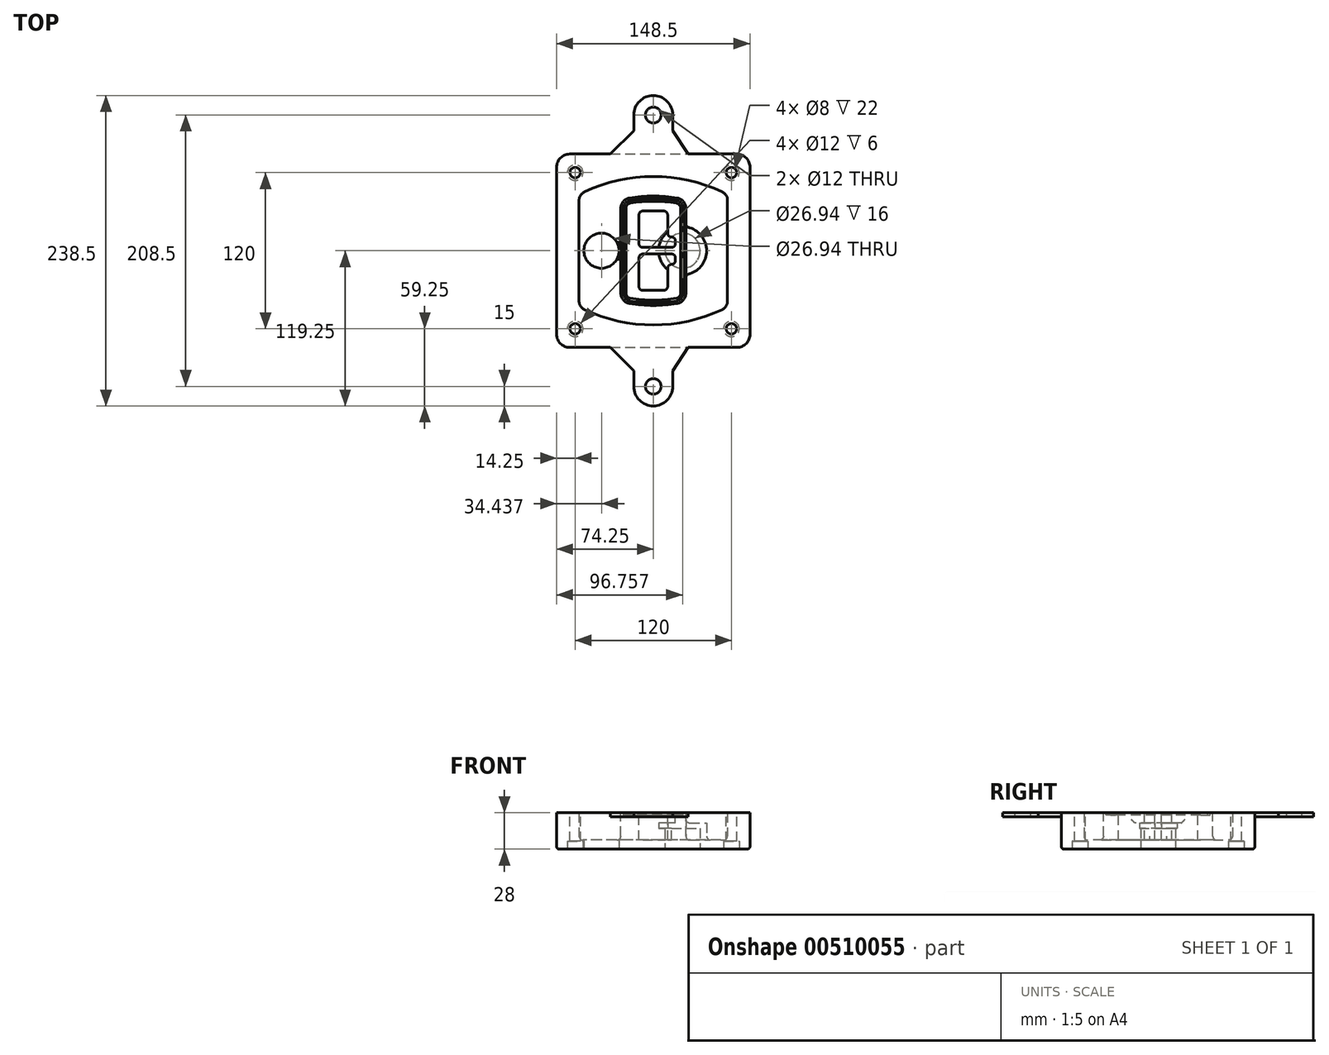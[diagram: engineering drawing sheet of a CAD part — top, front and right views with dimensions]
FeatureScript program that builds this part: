
annotation { "Feature Type Name" : "Feature", "Feature Type Description" : "" }
export const myFeature = defineFeature(function(context is Context, id is Id, definition is map)
    precondition{}
    {
        {
            var Q0;
            Q0=qCreatedBy(makeId("Top.planeOp"),FACE);
            var sketch = newSketch(context, id + "F0", { "sketchPlane" : qUnion([Q0])});
            skPoint(sketch, "E0.rect.middle", {"position": v(0, 0) * mm});
            skLineSegment(sketch, "E1.bottom", {"start": v(-64.25, -74.25) * mm, "end": v(64.25, -74.25) * mm});
            skLineSegment(sketch, "E1.top", {"start": v(-64.25, 74.25) * mm, "end": v(64.25, 74.25) * mm});
            skLineSegment(sketch, "E1.left", {"start": v(-74.25, -64.25) * mm, "end": v(-74.25, 64.25) * mm});
            skLineSegment(sketch, "E1.right", {"start": v(74.25, -64.25) * mm, "end": v(74.25, 64.25) * mm});
            skLineSegment(sketch, "E2", {"start": v(-74.25, 74.25) * mm, "end": v(74.25, -74.25) * mm, "construction": true});
            skLineSegment(sketch, "E3", {"start": v(74.25, 74.25) * mm, "end": v(-74.25, -74.25) * mm, "construction": true});
            skCircle(sketch, "E4", {"center": v(-60, 60) * mm, "radius": 4 * mm});
            skCircle(sketch, "E5", {"center": v(60, 60) * mm, "radius": 4 * mm});
            skCircle(sketch, "E6", {"center": v(60, -60) * mm, "radius": 4 * mm});
            skCircle(sketch, "E7", {"center": v(-60, -60) * mm, "radius": 4 * mm});
            skLineSegment(sketch, "E8", {"start": v(-60, 60) * mm, "end": v(60, 60) * mm, "construction": true});
            skLineSegment(sketch, "E9", {"start": v(60, 60) * mm, "end": v(60, -60) * mm, "construction": true});
            skLineSegment(sketch, "E10", {"start": v(60, -60) * mm, "end": v(-60, -60) * mm, "construction": true});
            skLineSegment(sketch, "E11", {"start": v(-60, -60) * mm, "end": v(-60, 60) * mm, "construction": true});
            skLineSegment(sketch, "E12", {"start": v(-60, 38.83) * mm, "end": v(-60, -38.83) * mm});
            skLineSegment(sketch, "E13", {"start": v(60, 38.83) * mm, "end": v(60, -38.83) * mm});
            skArc(sketch, "E14", {"start": v(54.26, 47.88) * mm, "mid": v(0, 60) * mm, "end": v(-54.26, 47.88) * mm});
            skArc(sketch, "E15", {"start": v(-54.26, -47.88) * mm, "mid": v(0, -60) * mm, "end": v(54.26, -47.88) * mm});
            skLineSegment(sketch, "E16", {"start": v(-60, 0) * mm, "end": v(60, 0) * mm, "construction": true});
            skPoint(sketch, "E17.visualSharp", {"position": v(-60, -45) * mm});
            skArc(sketch, "E17.filletArc", {"start": v(-60, -38.83) * mm, "mid": v(-58.44, -44.2) * mm, "end": v(-54.26, -47.88) * mm});
            skPoint(sketch, "E18.visualSharp", {"position": v(-60, 45) * mm});
            skArc(sketch, "E18.filletArc", {"start": v(-54.26, 47.88) * mm, "mid": v(-58.44, 44.2) * mm, "end": v(-60, 38.83) * mm});
            skPoint(sketch, "E19.visualSharp", {"position": v(60, 45) * mm});
            skArc(sketch, "E19.filletArc", {"start": v(60, 38.83) * mm, "mid": v(58.44, 44.2) * mm, "end": v(54.26, 47.88) * mm});
            skPoint(sketch, "E20.visualSharp", {"position": v(60, -45) * mm});
            skArc(sketch, "E20.filletArc", {"start": v(54.26, -47.88) * mm, "mid": v(58.44, -44.2) * mm, "end": v(60, -38.83) * mm});
            skPoint(sketch, "E21.visualSharp", {"position": v(-74.25, 74.25) * mm});
            skArc(sketch, "E21.filletArc", {"start": v(-64.25, 74.25) * mm, "mid": v(-71.32, 71.32) * mm, "end": v(-74.25, 64.25) * mm});
            skPoint(sketch, "E22.visualSharp", {"position": v(74.25, 74.25) * mm});
            skArc(sketch, "E22.filletArc", {"start": v(74.25, 64.25) * mm, "mid": v(71.32, 71.32) * mm, "end": v(64.25, 74.25) * mm});
            skPoint(sketch, "E23.visualSharp", {"position": v(74.25, -74.25) * mm});
            skArc(sketch, "E23.filletArc", {"start": v(64.25, -74.25) * mm, "mid": v(71.32, -71.32) * mm, "end": v(74.25, -64.25) * mm});
            skPoint(sketch, "E24.visualSharp", {"position": v(-74.25, -74.25) * mm});
            skArc(sketch, "E24.filletArc", {"start": v(-74.25, -64.25) * mm, "mid": v(-71.32, -71.32) * mm, "end": v(-64.25, -74.25) * mm});
            skArc(sketch, "E25.0", {"start": v(57, 38.83) * mm, "mid": v(55.9, 42.58) * mm, "end": v(52.98, 45.17) * mm});
            skLineSegment(sketch, "E25.1", {"start": v(57, 38.83) * mm, "end": v(57, -38.83) * mm});
            skArc(sketch, "E25.2", {"start": v(52.98, -45.17) * mm, "mid": v(55.9, -42.58) * mm, "end": v(57, -38.83) * mm});
            skArc(sketch, "E25.3", {"start": v(-52.98, -45.17) * mm, "mid": v(0, -57) * mm, "end": v(52.98, -45.17) * mm});
            skArc(sketch, "E25.4", {"start": v(-57, -38.83) * mm, "mid": v(-55.9, -42.58) * mm, "end": v(-52.98, -45.17) * mm});
            skArc(sketch, "E25.5", {"start": v(52.98, 45.17) * mm, "mid": v(0, 57) * mm, "end": v(-52.98, 45.17) * mm});
            skLineSegment(sketch, "E25.6", {"start": v(-57, 38.83) * mm, "end": v(-57, -38.83) * mm});
            skArc(sketch, "E25.7", {"start": v(-52.98, 45.17) * mm, "mid": v(-55.9, 42.58) * mm, "end": v(-57, 38.83) * mm});
            skArc(sketch, "E26.0", {"start": v(-55.96, 51.5) * mm, "mid": v(-61.82, 46.33) * mm, "end": v(-64, 38.83) * mm});
            skArc(sketch, "E26.1", {"start": v(55.96, 51.5) * mm, "mid": v(0, 64) * mm, "end": v(-55.96, 51.5) * mm});
            skArc(sketch, "E26.2", {"start": v(64, 38.83) * mm, "mid": v(61.82, 46.33) * mm, "end": v(55.96, 51.5) * mm});
            skLineSegment(sketch, "E26.3", {"start": v(64, 38.83) * mm, "end": v(64, -38.83) * mm});
            skArc(sketch, "E26.4", {"start": v(55.96, -51.5) * mm, "mid": v(61.82, -46.33) * mm, "end": v(64, -38.83) * mm});
            skLineSegment(sketch, "E26.5", {"start": v(-64, 38.83) * mm, "end": v(-64, -38.83) * mm});
            skArc(sketch, "E26.6", {"start": v(-55.96, -51.5) * mm, "mid": v(0, -64) * mm, "end": v(55.96, -51.5) * mm});
            skArc(sketch, "E26.7", {"start": v(-64, -38.83) * mm, "mid": v(-61.82, -46.33) * mm, "end": v(-55.96, -51.5) * mm});
            skSolve(sketch);
        }
        {
            var Q0;
            Q0=makeQuery(id+"F0.imprint","IMPRINT",FACE,{"disambiguationData":[TD([[makeQuery(id+"F0.imprint","IMPRINT",EDGE,{"derivedFrom":sQuery(id+"F0.wireOp",EDGE,"E1.bottom")}),1.0]])]});
            var Q1;
            Q1=makeQuery(id+"F0.imprint","IMPRINT",FACE,{"disambiguationData":[TD([[makeQuery(id+"F0.imprint","IMPRINT",EDGE,{"derivedFrom":sQuery(id+"F0.wireOp",EDGE,"E12")}),1.0]])]});
            var Q2;
            Q2=makeQuery(id+"F0.imprint","IMPRINT",FACE,{"disambiguationData":[TD([[makeQuery(id+"F0.imprint","IMPRINT",EDGE,{"derivedFrom":sQuery(id+"F0.wireOp",EDGE,"E25.0")}),1.0]])]});
            var Q3;
            Q3=makeQuery(id+"F0.imprint","IMPRINT",FACE,{"disambiguationData":[TD([[makeQuery(id+"F0.imprint","IMPRINT",EDGE,{"derivedFrom":sQuery(id+"F0.wireOp",EDGE,"E12")}),-1.0]])]});
            extrude(context, id + "F1", {"entities" : qUnion([Q0, Q1, Q2, Q3]), "oppositeDirection" : true, "depth" : 25 * mm});
        }
        {
            var Q0;
            Q0=makeQuery(id+"F0.imprint","IMPRINT",FACE,{"disambiguationData":[TD([[makeQuery(id+"F0.imprint","IMPRINT",EDGE,{"derivedFrom":sQuery(id+"F0.wireOp",EDGE,"E12")}),1.0]])]});
            extrude(context, id + "F2", {"entities" : qUnion([Q0]), "operationType" : NewBodyOperationType.ADD, "depth" : 3 * mm});
        }
        {
            var Q0;
            Q0=makeQuery(id+"F0.imprint","IMPRINT",FACE,{"disambiguationData":[TD([[makeQuery(id+"F0.imprint","IMPRINT",EDGE,{"derivedFrom":sQuery(id+"F0.wireOp",EDGE,"E25.0")}),1.0]])]});
            extrude(context, id + "F3", {"entities" : qUnion([Q0]), "operationType" : NewBodyOperationType.REMOVE, "oppositeDirection" : true, "depth" : 18 * mm});
        }
        {
            var Q0;
            Q0=makeQuery(id+"F2.opExtrude","CAP_FACE",FACE,{"disambiguationData":[OSD([sQuery(id+"F0.wireOp",EDGE,"E12"),sQuery(id+"F0.wireOp",EDGE,"E13"),sQuery(id+"F0.wireOp",EDGE,"E14"),sQuery(id+"F0.wireOp",EDGE,"E15"),sQuery(id+"F0.wireOp",EDGE,"E17.filletArc"),sQuery(id+"F0.wireOp",EDGE,"E18.filletArc"),sQuery(id+"F0.wireOp",EDGE,"E19.filletArc"),sQuery(id+"F0.wireOp",EDGE,"E20.filletArc"),sQuery(id+"F0.wireOp",EDGE,"E25.0"),sQuery(id+"F0.wireOp",EDGE,"E25.1"),sQuery(id+"F0.wireOp",EDGE,"E25.2"),sQuery(id+"F0.wireOp",EDGE,"E25.3"),sQuery(id+"F0.wireOp",EDGE,"E25.4"),sQuery(id+"F0.wireOp",EDGE,"E25.5"),sQuery(id+"F0.wireOp",EDGE,"E25.6"),sQuery(id+"F0.wireOp",EDGE,"E25.7")])],"isStart":false});
            var sketch = newSketch(context, id + "F4", { "sketchPlane" : qUnion([Q0])});
            skArc(sketch, "E27.0", {"start": v(-18.34, -40.45) * mm, "mid": v(0, -42) * mm, "end": v(18.34, -40.45) * mm});
            skArc(sketch, "E28.0", {"start": v(18.34, 40.45) * mm, "mid": v(0, 42) * mm, "end": v(-18.34, 40.45) * mm});
            skLineSegment(sketch, "E29", {"start": v(-25, 32.57) * mm, "end": v(-25, -32.57) * mm});
            skLineSegment(sketch, "E30", {"start": v(25, 32.57) * mm, "end": v(25, -32.57) * mm});
            skLineSegment(sketch, "E31", {"start": v(-25, 39.1) * mm, "end": v(25, 39.1) * mm, "construction": true});
            skLineSegment(sketch, "E32", {"start": v(-25, -39.1) * mm, "end": v(25, -39.1) * mm, "construction": true});
            skPoint(sketch, "E33.visualSharp", {"position": v(-25, 39.1) * mm});
            skArc(sketch, "E33.filletArc", {"start": v(-18.34, 40.45) * mm, "mid": v(-23.11, 37.73) * mm, "end": v(-25, 32.57) * mm});
            skPoint(sketch, "E34.visualSharp", {"position": v(25, 39.1) * mm});
            skArc(sketch, "E34.filletArc", {"start": v(25, 32.57) * mm, "mid": v(23.11, 37.73) * mm, "end": v(18.34, 40.45) * mm});
            skPoint(sketch, "E35.visualSharp", {"position": v(25, -39.1) * mm});
            skArc(sketch, "E35.filletArc", {"start": v(18.34, -40.45) * mm, "mid": v(23.11, -37.73) * mm, "end": v(25, -32.57) * mm});
            skPoint(sketch, "E36.visualSharp", {"position": v(-25, -39.1) * mm});
            skArc(sketch, "E36.filletArc", {"start": v(-25, -32.57) * mm, "mid": v(-23.11, -37.73) * mm, "end": v(-18.34, -40.45) * mm});
            skArc(sketch, "E37.0", {"start": v(52.98, 45.17) * mm, "mid": v(0, 57) * mm, "end": v(-52.98, 45.17) * mm});
            skArc(sketch, "E37.1", {"start": v(-52.98, 45.17) * mm, "mid": v(-55.9, 42.58) * mm, "end": v(-57, 38.83) * mm});
            skLineSegment(sketch, "E37.2", {"start": v(-57, 38.83) * mm, "end": v(-57, -38.83) * mm});
            skArc(sketch, "E37.3", {"start": v(-57, -38.83) * mm, "mid": v(-55.9, -42.58) * mm, "end": v(-52.98, -45.17) * mm});
            skArc(sketch, "E37.4", {"start": v(-52.98, -45.17) * mm, "mid": v(0, -57) * mm, "end": v(52.98, -45.17) * mm});
            skArc(sketch, "E37.5", {"start": v(52.98, -45.17) * mm, "mid": v(55.9, -42.58) * mm, "end": v(57, -38.83) * mm});
            skLineSegment(sketch, "E37.6", {"start": v(57, 38.83) * mm, "end": v(57, -38.83) * mm});
            skArc(sketch, "E37.7", {"start": v(57, 38.83) * mm, "mid": v(55.9, 42.58) * mm, "end": v(52.98, 45.17) * mm});
            skLineSegment(sketch, "E38.0", {"start": v(23, 32.57) * mm, "end": v(23, -32.57) * mm});
            skArc(sketch, "E38.1", {"start": v(18, -38.48) * mm, "mid": v(21.58, -36.44) * mm, "end": v(23, -32.57) * mm});
            skArc(sketch, "E38.2", {"start": v(-18, -38.48) * mm, "mid": v(0, -40) * mm, "end": v(18, -38.48) * mm});
            skArc(sketch, "E38.3", {"start": v(-23, -32.57) * mm, "mid": v(-21.58, -36.44) * mm, "end": v(-18, -38.48) * mm});
            skLineSegment(sketch, "E38.4", {"start": v(-23, 32.57) * mm, "end": v(-23, -32.57) * mm});
            skArc(sketch, "E38.5", {"start": v(23, 32.57) * mm, "mid": v(21.58, 36.44) * mm, "end": v(18, 38.48) * mm});
            skArc(sketch, "E38.6", {"start": v(-18, 38.48) * mm, "mid": v(-21.58, 36.44) * mm, "end": v(-23, 32.57) * mm});
            skArc(sketch, "E38.7", {"start": v(18, 38.48) * mm, "mid": v(0, 40) * mm, "end": v(-18, 38.48) * mm});
            skArc(sketch, "E39.0", {"start": v(21, 32.57) * mm, "mid": v(20.06, 35.15) * mm, "end": v(17.67, 36.5) * mm});
            skLineSegment(sketch, "E39.1", {"start": v(21, 32.57) * mm, "end": v(21, -32.57) * mm});
            skArc(sketch, "E39.2", {"start": v(17.67, -36.5) * mm, "mid": v(20.06, -35.15) * mm, "end": v(21, -32.57) * mm});
            skArc(sketch, "E39.3", {"start": v(-17.67, -36.5) * mm, "mid": v(0, -38) * mm, "end": v(17.67, -36.5) * mm});
            skArc(sketch, "E39.4", {"start": v(-21, -32.57) * mm, "mid": v(-20.06, -35.15) * mm, "end": v(-17.67, -36.5) * mm});
            skArc(sketch, "E39.5", {"start": v(17.67, 36.5) * mm, "mid": v(0, 38) * mm, "end": v(-17.67, 36.5) * mm});
            skLineSegment(sketch, "E39.6", {"start": v(-21, 32.57) * mm, "end": v(-21, -32.57) * mm});
            skArc(sketch, "E39.7", {"start": v(-17.67, 36.5) * mm, "mid": v(-20.06, 35.15) * mm, "end": v(-21, 32.57) * mm});
            skLineSegment(sketch, "E40", {"start": v(-25, 0) * mm, "end": v(25, 0) * mm, "construction": true});
            skLineSegment(sketch, "E41", {"start": v(-11, 5.5) * mm, "end": v(-11, 27.5) * mm});
            skLineSegment(sketch, "E42", {"start": v(-8, 30.5) * mm, "end": v(8, 30.5) * mm});
            skLineSegment(sketch, "E43", {"start": v(11, 27.5) * mm, "end": v(11, 13.5) * mm});
            skLineSegment(sketch, "E44", {"start": v(14, 10.5) * mm, "end": v(14, 10.5) * mm});
            skLineSegment(sketch, "E45", {"start": v(17, 7.5) * mm, "end": v(17, 5.5) * mm});
            skLineSegment(sketch, "E46", {"start": v(14, 2.5) * mm, "end": v(-8, 2.5) * mm});
            skPoint(sketch, "E47.visualSharp", {"position": v(-11, 30.5) * mm});
            skArc(sketch, "E47.filletArc", {"start": v(-8, 30.5) * mm, "mid": v(-10.12, 29.62) * mm, "end": v(-11, 27.5) * mm});
            skPoint(sketch, "E48.visualSharp", {"position": v(11, 30.5) * mm});
            skArc(sketch, "E48.filletArc", {"start": v(11, 27.5) * mm, "mid": v(10.12, 29.62) * mm, "end": v(8, 30.5) * mm});
            skPoint(sketch, "E49.visualSharp", {"position": v(11, 10.5) * mm});
            skArc(sketch, "E49.filletArc", {"start": v(11, 13.5) * mm, "mid": v(11.88, 11.38) * mm, "end": v(14, 10.5) * mm});
            skPoint(sketch, "E50.visualSharp", {"position": v(17, 10.5) * mm});
            skArc(sketch, "E50.filletArc", {"start": v(17, 7.5) * mm, "mid": v(16.12, 9.62) * mm, "end": v(14, 10.5) * mm});
            skPoint(sketch, "E51.visualSharp", {"position": v(17, 2.5) * mm});
            skArc(sketch, "E51.filletArc", {"start": v(14, 2.5) * mm, "mid": v(16.12, 3.38) * mm, "end": v(17, 5.5) * mm});
            skPoint(sketch, "E52.visualSharp", {"position": v(-11, 2.5) * mm});
            skArc(sketch, "E52.filletArc", {"start": v(-11, 5.5) * mm, "mid": v(-10.12, 3.38) * mm, "end": v(-8, 2.5) * mm});
            skLineSegment(sketch, "E53.0.MirrorCS", {"start": v(14, -2.5) * mm, "end": v(-8, -2.5) * mm});
            skArc(sketch, "E54.0.MirrorCS", {"start": v(-11, -5.5) * mm, "mid": v(-10.12, -3.38) * mm, "end": v(-8, -2.5) * mm});
            skLineSegment(sketch, "E55.0.MirrorCS", {"start": v(-11, -5.5) * mm, "end": v(-11, -27.5) * mm});
            skArc(sketch, "E56.0.MirrorCS", {"start": v(-8, -30.5) * mm, "mid": v(-10.12, -29.62) * mm, "end": v(-11, -27.5) * mm});
            skLineSegment(sketch, "E57.0.MirrorCS", {"start": v(-8, -30.5) * mm, "end": v(8, -30.5) * mm});
            skArc(sketch, "E58.0.MirrorCS", {"start": v(11, -27.5) * mm, "mid": v(10.12, -29.62) * mm, "end": v(8, -30.5) * mm});
            skLineSegment(sketch, "E59.0.MirrorCS", {"start": v(11, -27.5) * mm, "end": v(11, -13.5) * mm});
            skArc(sketch, "E60.0.MirrorCS", {"start": v(11, -13.5) * mm, "mid": v(11.88, -11.38) * mm, "end": v(14, -10.5) * mm});
            skArc(sketch, "E61.0.MirrorCS", {"start": v(17, -7.5) * mm, "mid": v(16.12, -9.62) * mm, "end": v(14, -10.5) * mm});
            skLineSegment(sketch, "E62.0.MirrorCS", {"start": v(17, -7.5) * mm, "end": v(17, -5.5) * mm});
            skArc(sketch, "E63.0.MirrorCS", {"start": v(14, -2.5) * mm, "mid": v(16.12, -3.38) * mm, "end": v(17, -5.5) * mm});
            skSolve(sketch);
        }
        {
            var Q0;
            Q0=makeQuery(id+"F4.imprint","IMPRINT",FACE,{"disambiguationData":[TD([[makeQuery(id+"F4.imprint","IMPRINT",EDGE,{"derivedFrom":sQuery(id+"F4.wireOp",EDGE,"E27.0")}),1.0]])]});
            var Q1;
            Q1=makeQuery(id+"F4.imprint","IMPRINT",FACE,{"disambiguationData":[TD([[makeQuery(id+"F4.imprint","IMPRINT",EDGE,{"derivedFrom":sQuery(id+"F4.wireOp",EDGE,"E38.0")}),-1.0]])]});
            var Q2;
            Q2=makeQuery(id+"F4.imprint","IMPRINT",FACE,{"disambiguationData":[TD([[makeQuery(id+"F4.imprint","IMPRINT",EDGE,{"derivedFrom":sQuery(id+"F4.wireOp",EDGE,"E39.0")}),1.0]])]});
            extrude(context, id + "F5", {"entities" : qUnion([Q0, Q1, Q2]), "operationType" : NewBodyOperationType.ADD, "endBound" : BoundingType.UP_TO_NEXT, "oppositeDirection" : true, "depth" : 25 * mm});
        }
        {
            var Q0;
            Q0=makeQuery(id+"F4.imprint","IMPRINT",FACE,{"disambiguationData":[TD([[makeQuery(id+"F4.imprint","IMPRINT",EDGE,{"derivedFrom":sQuery(id+"F4.wireOp",EDGE,"E38.0")}),-1.0]])]});
            extrude(context, id + "F6", {"entities" : qUnion([Q0]), "operationType" : NewBodyOperationType.REMOVE, "oppositeDirection" : true, "depth" : 2 * mm});
        }
        {
            var Q0;
            Q0=makeQuery(id+"F1.opExtrude","CAP_FACE",FACE,{"disambiguationData":[OSD([sQuery(id+"F0.wireOp",EDGE,"E1.bottom"),sQuery(id+"F0.wireOp",EDGE,"E1.top"),sQuery(id+"F0.wireOp",EDGE,"E1.left"),sQuery(id+"F0.wireOp",EDGE,"E1.right"),sQuery(id+"F0.wireOp",EDGE,"E4"),sQuery(id+"F0.wireOp",EDGE,"E5"),sQuery(id+"F0.wireOp",EDGE,"E6"),sQuery(id+"F0.wireOp",EDGE,"E7"),sQuery(id+"F0.wireOp",EDGE,"E21.filletArc"),sQuery(id+"F0.wireOp",EDGE,"E22.filletArc"),sQuery(id+"F0.wireOp",EDGE,"E23.filletArc"),sQuery(id+"F0.wireOp",EDGE,"E24.filletArc")])],"isStart":false});
            var sketch = newSketch(context, id + "F7", { "sketchPlane" : qUnion([Q0])});
            skCircle(sketch, "E64", {"center": v(22.5, 0) * mm, "radius": 13.47 * mm});
            skCircle(sketch, "E65", {"center": v(-39.81, 0) * mm, "radius": 13.47 * mm});
            skLineSegment(sketch, "E66", {"start": v(74.25, 0) * mm, "end": v(-74.25, 0) * mm});
            skCircle(sketch, "E67", {"center": v(22.5, 0) * mm, "radius": 18.47 * mm});
            skCircle(sketch, "E68", {"center": v(60, -60) * mm, "radius": 6 * mm});
            skCircle(sketch, "E69", {"center": v(-60, -60) * mm, "radius": 6 * mm});
            skCircle(sketch, "E70", {"center": v(-60, 60) * mm, "radius": 6 * mm});
            skCircle(sketch, "E71", {"center": v(60, 60) * mm, "radius": 6 * mm});
            skSolve(sketch);
        }
        {
            var Q0;
            {var subQ1=sQuery(id+"F7.wireOp",EDGE,"E66");var subQ4=sQuery(id+"F7.wireOp",EDGE,"E64");var subQ6=makeQuery(id+"F7.imprint","INTERSECT",VERTEX,{"disambiguationData":[OD(0.0)],"derivedFrom":[subQ4,subQ1]});Q0=makeQuery(id+"F7.imprint","IMPRINT",FACE,{"disambiguationData":[TD([[makeQuery(id+"F7.imprint","IMPRINT",EDGE,{"disambiguationData":[TD([[subQ6,-1.0]])],"derivedFrom":subQ4}),-1.0]])]});}
            var Q1;
            {var subQ0=sQuery(id+"F7.wireOp",EDGE,"E66");var subQ1=sQuery(id+"F7.wireOp",EDGE,"E64");var subQ3=makeQuery(id+"F7.imprint","INTERSECT",VERTEX,{"disambiguationData":[OD(0.0)],"derivedFrom":[subQ1,subQ0]});Q1=makeQuery(id+"F7.imprint","IMPRINT",FACE,{"disambiguationData":[TD([[makeQuery(id+"F7.imprint","IMPRINT",EDGE,{"disambiguationData":[TD([[subQ3,-1.0]])],"derivedFrom":subQ1}),1.0]])]});}
            var Q2;
            {var subQ0=sQuery(id+"F7.wireOp",EDGE,"E66");var subQ1=sQuery(id+"F7.wireOp",EDGE,"E64");var subQ3=makeQuery(id+"F7.imprint","INTERSECT",VERTEX,{"disambiguationData":[OD(0.0)],"derivedFrom":[subQ1,subQ0]});Q2=makeQuery(id+"F7.imprint","IMPRINT",FACE,{"disambiguationData":[TD([[makeQuery(id+"F7.imprint","IMPRINT",EDGE,{"disambiguationData":[TD([[subQ3,1.0]])],"derivedFrom":subQ1}),1.0]])]});}
            var Q3;
            {var subQ1=sQuery(id+"F7.wireOp",EDGE,"E66");var subQ4=sQuery(id+"F7.wireOp",EDGE,"E64");var subQ6=makeQuery(id+"F7.imprint","INTERSECT",VERTEX,{"disambiguationData":[OD(0.0)],"derivedFrom":[subQ4,subQ1]});Q3=makeQuery(id+"F7.imprint","IMPRINT",FACE,{"disambiguationData":[TD([[makeQuery(id+"F7.imprint","IMPRINT",EDGE,{"disambiguationData":[TD([[subQ6,1.0]])],"derivedFrom":subQ4}),-1.0]])]});}
            extrude(context, id + "F8", {"entities" : qUnion([Q0, Q1, Q2, Q3]), "operationType" : NewBodyOperationType.ADD, "oppositeDirection" : true, "depth" : 20 * mm});
        }
        {
            var Q0;
            {var subQ0=sQuery(id+"F7.wireOp",EDGE,"E66");var subQ1=sQuery(id+"F7.wireOp",EDGE,"E64");var subQ3=makeQuery(id+"F7.imprint","INTERSECT",VERTEX,{"disambiguationData":[OD(0.0)],"derivedFrom":[subQ1,subQ0]});Q0=makeQuery(id+"F7.imprint","IMPRINT",FACE,{"disambiguationData":[TD([[makeQuery(id+"F7.imprint","IMPRINT",EDGE,{"disambiguationData":[TD([[subQ3,-1.0]])],"derivedFrom":subQ1}),1.0]])]});}
            var Q1;
            {var subQ0=sQuery(id+"F7.wireOp",EDGE,"E66");var subQ1=sQuery(id+"F7.wireOp",EDGE,"E64");var subQ3=makeQuery(id+"F7.imprint","INTERSECT",VERTEX,{"disambiguationData":[OD(0.0)],"derivedFrom":[subQ1,subQ0]});Q1=makeQuery(id+"F7.imprint","IMPRINT",FACE,{"disambiguationData":[TD([[makeQuery(id+"F7.imprint","IMPRINT",EDGE,{"disambiguationData":[TD([[subQ3,1.0]])],"derivedFrom":subQ1}),1.0]])]});}
            extrude(context, id + "F9", {"entities" : qUnion([Q0, Q1]), "operationType" : NewBodyOperationType.REMOVE, "oppositeDirection" : true, "depth" : 16 * mm});
        }
        {
            var Q0;
            {var subQ0=sQuery(id+"F7.wireOp",EDGE,"E66");var subQ1=sQuery(id+"F7.wireOp",EDGE,"E65");var subQ3=makeQuery(id+"F7.imprint","INTERSECT",VERTEX,{"disambiguationData":[OD(0.0)],"derivedFrom":[subQ1,subQ0]});Q0=makeQuery(id+"F7.imprint","IMPRINT",FACE,{"disambiguationData":[TD([[makeQuery(id+"F7.imprint","IMPRINT",EDGE,{"disambiguationData":[TD([[subQ3,-1.0]])],"derivedFrom":subQ1}),1.0]])]});}
            var Q1;
            {var subQ0=sQuery(id+"F7.wireOp",EDGE,"E66");var subQ1=sQuery(id+"F7.wireOp",EDGE,"E65");var subQ3=makeQuery(id+"F7.imprint","INTERSECT",VERTEX,{"disambiguationData":[OD(0.0)],"derivedFrom":[subQ1,subQ0]});Q1=makeQuery(id+"F7.imprint","IMPRINT",FACE,{"disambiguationData":[TD([[makeQuery(id+"F7.imprint","IMPRINT",EDGE,{"disambiguationData":[TD([[subQ3,1.0]])],"derivedFrom":subQ1}),1.0]])]});}
            extrude(context, id + "F10", {"entities" : qUnion([Q0, Q1]), "operationType" : NewBodyOperationType.REMOVE, "oppositeDirection" : true, "depth" : 25 * mm});
        }
        {
            var Q0;
            Q0=makeQuery(id+"F7.imprint","IMPRINT",FACE,{"disambiguationData":[TD([[makeQuery(id+"F7.imprint","IMPRINT",EDGE,{"derivedFrom":sQuery(id+"F7.wireOp",EDGE,"E68")}),1.0]])]});
            var Q1;
            Q1=makeQuery(id+"F7.imprint","IMPRINT",FACE,{"disambiguationData":[TD([[makeQuery(id+"F7.imprint","IMPRINT",EDGE,{"derivedFrom":makeQuery(id+"F1.opExtrude","CAP_EDGE",EDGE,{"disambiguationData":[OSD([sQuery(id+"F0.wireOp",EDGE,"E5")])],"isStart":false})}),-1.0]])]});
            var Q2;
            Q2=makeQuery(id+"F7.imprint","IMPRINT",FACE,{"disambiguationData":[TD([[makeQuery(id+"F7.imprint","IMPRINT",EDGE,{"derivedFrom":sQuery(id+"F7.wireOp",EDGE,"E69")}),1.0]])]});
            var Q3;
            Q3=makeQuery(id+"F7.imprint","IMPRINT",FACE,{"disambiguationData":[TD([[makeQuery(id+"F7.imprint","IMPRINT",EDGE,{"derivedFrom":makeQuery(id+"F1.opExtrude","CAP_EDGE",EDGE,{"disambiguationData":[OSD([sQuery(id+"F0.wireOp",EDGE,"E4")])],"isStart":false})}),-1.0]])]});
            var Q4;
            Q4=makeQuery(id+"F7.imprint","IMPRINT",FACE,{"disambiguationData":[TD([[makeQuery(id+"F7.imprint","IMPRINT",EDGE,{"derivedFrom":sQuery(id+"F7.wireOp",EDGE,"E70")}),1.0]])]});
            var Q5;
            Q5=makeQuery(id+"F7.imprint","IMPRINT",FACE,{"disambiguationData":[TD([[makeQuery(id+"F7.imprint","IMPRINT",EDGE,{"derivedFrom":makeQuery(id+"F1.opExtrude","CAP_EDGE",EDGE,{"disambiguationData":[OSD([sQuery(id+"F0.wireOp",EDGE,"E7")])],"isStart":false})}),-1.0]])]});
            var Q6;
            Q6=makeQuery(id+"F7.imprint","IMPRINT",FACE,{"disambiguationData":[TD([[makeQuery(id+"F7.imprint","IMPRINT",EDGE,{"derivedFrom":sQuery(id+"F7.wireOp",EDGE,"E71")}),1.0]])]});
            var Q7;
            Q7=makeQuery(id+"F7.imprint","IMPRINT",FACE,{"disambiguationData":[TD([[makeQuery(id+"F7.imprint","IMPRINT",EDGE,{"derivedFrom":makeQuery(id+"F1.opExtrude","CAP_EDGE",EDGE,{"disambiguationData":[OSD([sQuery(id+"F0.wireOp",EDGE,"E6")])],"isStart":false})}),-1.0]])]});
            extrude(context, id + "F11", {"entities" : qUnion([Q0, Q1, Q2, Q3, Q4, Q5, Q6, Q7]), "operationType" : NewBodyOperationType.REMOVE, "oppositeDirection" : true, "depth" : 6 * mm});
        }
        {
            var Q0;
            Q0=makeQuery(id+"F9.boolean.opBoolean","COPY",FACE,{"derivedFrom":makeQuery(id+"F9.opExtrude","CAP_FACE",FACE,{"disambiguationData":[OSD([sQuery(id+"F7.wireOp",EDGE,"E64")])],"isStart":false})});
            var sketch = newSketch(context, id + "F12", { "sketchPlane" : qUnion([Q0])});
            skArc(sketch, "E72.0", {"start": v(11, 14.45) * mm, "mid": v(6.45, 9.13) * mm, "end": v(4.2, 2.5) * mm});
            skArc(sketch, "E72.1", {"start": v(4.2, -2.5) * mm, "mid": v(6.45, -9.13) * mm, "end": v(11, -14.45) * mm});
            skLineSegment(sketch, "E73", {"start": v(4.2, -2.5) * mm, "end": v(14, -2.5) * mm});
            skLineSegment(sketch, "E74.0", {"start": v(14, 2.5) * mm, "end": v(4.2, 2.5) * mm});
            skArc(sketch, "E74.1", {"start": v(14, 2.5) * mm, "mid": v(16.12, 3.38) * mm, "end": v(17, 5.5) * mm});
            skLineSegment(sketch, "E74.2", {"start": v(17, 7.5) * mm, "end": v(17, 5.5) * mm});
            skArc(sketch, "E74.3", {"start": v(17, 7.5) * mm, "mid": v(16.12, 9.62) * mm, "end": v(14, 10.5) * mm});
            skArc(sketch, "E74.4", {"start": v(11, 13.5) * mm, "mid": v(11.88, 11.38) * mm, "end": v(14, 10.5) * mm});
            skLineSegment(sketch, "E74.5", {"start": v(11, 14.45) * mm, "end": v(11, 13.5) * mm});
            skLineSegment(sketch, "E74.7", {"start": v(14, -2.5) * mm, "end": v(4.2, -2.5) * mm});
            skArc(sketch, "E74.8", {"start": v(14, -2.5) * mm, "mid": v(16.12, -3.38) * mm, "end": v(17, -5.5) * mm});
            skLineSegment(sketch, "E74.9", {"start": v(17, -7.5) * mm, "end": v(17, -5.5) * mm});
            skArc(sketch, "E74.10", {"start": v(17, -7.5) * mm, "mid": v(16.12, -9.62) * mm, "end": v(14, -10.5) * mm});
            skArc(sketch, "E74.11", {"start": v(11, -13.5) * mm, "mid": v(11.88, -11.38) * mm, "end": v(14, -10.5) * mm});
            skLineSegment(sketch, "E74.12", {"start": v(11, -14.45) * mm, "end": v(11, -13.5) * mm});
            skPoint(sketch, "E75.orphan", {"position": v(11, -27.5) * mm});
            skPoint(sketch, "E76.orphan", {"position": v(-8, -2.5) * mm});
            skPoint(sketch, "E77.orphan", {"position": v(-8, 2.5) * mm});
            skPoint(sketch, "E78.orphan", {"position": v(11, 27.5) * mm});
            skSolve(sketch);
        }
        {
            var Q0;
            {var subQ7=sQuery(id+"F12.wireOp",EDGE,"E72.0");var subQ14=sQuery(id+"F12.wireOp",EDGE,"E72.1");var subQ16=sQuery(id+"F12.wireOp",EDGE,"E74.1");var subQ18=sQuery(id+"F12.wireOp",EDGE,"E74.8");Q0=qUnion([makeQuery(id+"F12.imprint","IMPRINT",FACE,{"disambiguationData":[TD([[makeQuery(id+"F12.imprint","IMPRINT",EDGE,{"derivedFrom":subQ7}),1.0]])]}),makeQuery(id+"F12.imprint","IMPRINT",FACE,{"disambiguationData":[TD([[makeQuery(id+"F12.imprint","IMPRINT",EDGE,{"derivedFrom":subQ14}),1.0]])]}),makeQuery(id+"F12.imprint","IMPRINT",FACE,{"disambiguationData":[TD([[makeQuery(id+"F12.imprint","IMPRINT",EDGE,{"derivedFrom":subQ16}),1.0]])]}),makeQuery(id+"F12.imprint","IMPRINT",FACE,{"disambiguationData":[TD([[makeQuery(id+"F12.imprint","IMPRINT",EDGE,{"derivedFrom":subQ18}),-1.0]])]})]);}
            var Q1;
            Q1=makeQuery(id+"F5.boolean.opBoolean","SPLIT",FACE,{"disambiguationData":[TD([makeQuery(id+"F5.opExtrude","SWEPT_FACE",FACE,{"disambiguationData":[OSD([sQuery(id+"F4.wireOp",EDGE,"E41")])]})])],"derivedFrom":makeQuery(id+"F3.boolean.opBoolean","COPY",FACE,{"derivedFrom":makeQuery(id+"F3.opExtrude","CAP_FACE",FACE,{"disambiguationData":[OSD([sQuery(id+"F0.wireOp",EDGE,"E25.0"),sQuery(id+"F0.wireOp",EDGE,"E25.1"),sQuery(id+"F0.wireOp",EDGE,"E25.2"),sQuery(id+"F0.wireOp",EDGE,"E25.3"),sQuery(id+"F0.wireOp",EDGE,"E25.4"),sQuery(id+"F0.wireOp",EDGE,"E25.5"),sQuery(id+"F0.wireOp",EDGE,"E25.6"),sQuery(id+"F0.wireOp",EDGE,"E25.7")])],"isStart":false})})});
            extrude(context, id + "F13", {"entities" : qUnion([Q0]), "operationType" : NewBodyOperationType.REMOVE, "endBound" : BoundingType.UP_TO_SURFACE, "endBoundEntityFace" : qUnion([Q1]), "depth" : 25 * mm});
        }
        {
            var Q0;
            Q0=makeQuery(id+"F3.boolean.opBoolean","COPY",EDGE,{"derivedFrom":makeQuery(id+"F3.opExtrude","CAP_EDGE",EDGE,{"disambiguationData":[OSD([sQuery(id+"F0.wireOp",EDGE,"E25.6")])],"isStart":false})});
            var Q1;
            Q1=makeQuery(id+"F8.boolean.opBoolean","INTERSECT",EDGE,{"derivedFrom":[makeQuery(id+"F5.opExtrude","SWEPT_FACE",FACE,{"disambiguationData":[OSD([sQuery(id+"F4.wireOp",EDGE,"E30")])]}),makeQuery(id+"F8.opExtrude","CAP_FACE",FACE,{"disambiguationData":[OSD([sQuery(id+"F7.wireOp",EDGE,"E67")])],"isStart":false})]});
            var Q2;
            Q2=makeQuery(id+"F8.boolean.opBoolean","INTERSECT",EDGE,{"disambiguationData":[OD(1.0)],"derivedFrom":[makeQuery(id+"F5.opExtrude","SWEPT_FACE",FACE,{"disambiguationData":[OSD([sQuery(id+"F4.wireOp",EDGE,"E30")])]}),makeQuery(id+"F8.opExtrude","SWEPT_FACE",FACE,{"disambiguationData":[OSD([sQuery(id+"F7.wireOp",EDGE,"E67")])]})]});
            var Q3;
            {var subQ0=sQuery(id+"F4.wireOp",EDGE,"E30");Q3=makeQuery(id+"F8.boolean.opBoolean","SPLIT",EDGE,{"disambiguationData":[TD([makeQuery(id+"F5.opExtrude","SWEPT_FACE",FACE,{"disambiguationData":[OSD([sQuery(id+"F4.wireOp",EDGE,"E35.filletArc")])]})])],"derivedFrom":makeQuery(id+"F5.opExtrude","CAP_EDGE",EDGE,{"disambiguationData":[OSD([subQ0])],"isStart":false})});}
            var Q4;
            {var subQ0=sQuery(id+"F0.wireOp",EDGE,"E25.7");var subQ1=sQuery(id+"F0.wireOp",EDGE,"E25.1");var subQ2=sQuery(id+"F0.wireOp",EDGE,"E25.6");var subQ3=sQuery(id+"F0.wireOp",EDGE,"E25.5");var subQ4=sQuery(id+"F0.wireOp",EDGE,"E25.4");var subQ5=sQuery(id+"F0.wireOp",EDGE,"E25.0");var subQ6=sQuery(id+"F0.wireOp",EDGE,"E25.2");var subQ7=sQuery(id+"F0.wireOp",EDGE,"E25.3");Q4=makeQuery(id+"F8.boolean.opBoolean","INTERSECT",EDGE,{"derivedFrom":[makeQuery(id+"F5.boolean.opBoolean","SPLIT",FACE,{"disambiguationData":[TD([makeQuery(id+"F2.opExtrude","SWEPT_FACE",FACE,{"disambiguationData":[OSD([subQ5])]})])],"derivedFrom":makeQuery(id+"F3.boolean.opBoolean","COPY",FACE,{"derivedFrom":makeQuery(id+"F3.opExtrude","CAP_FACE",FACE,{"disambiguationData":[OSD([subQ5,subQ1,subQ6,subQ7,subQ4,subQ3,subQ2,subQ0])],"isStart":false})})}),makeQuery(id+"F8.opExtrude","SWEPT_FACE",FACE,{"disambiguationData":[OSD([sQuery(id+"F7.wireOp",EDGE,"E67")])]})]});}
            var Q5;
            Q5=makeQuery(id+"F8.boolean.opBoolean","INTERSECT",EDGE,{"disambiguationData":[OD(0.0)],"derivedFrom":[makeQuery(id+"F5.opExtrude","SWEPT_FACE",FACE,{"disambiguationData":[OSD([sQuery(id+"F4.wireOp",EDGE,"E30")])]}),makeQuery(id+"F8.opExtrude","SWEPT_FACE",FACE,{"disambiguationData":[OSD([sQuery(id+"F7.wireOp",EDGE,"E67")])]})]});
            fillet(context, id + "F14", {"entities" : qUnion([Q0, Q1, Q2, Q3, Q4, Q5]), "radius" : 3 * mm, "tangentPropagation" : true, "allowEdgeOverflow" : false});
        }
        {
            var Q0;
            Q0=makeQuery(id+"F1.opExtrude","CAP_EDGE",EDGE,{"disambiguationData":[OSD([sQuery(id+"F0.wireOp",EDGE,"E1.bottom")])],"isStart":false});
            fillet(context, id + "F15", {"entities" : qUnion([Q0]), "radius" : 2 * mm, "tangentPropagation" : true, "allowEdgeOverflow" : false});
        }
        {
            var Q0;
            {var subQ0=sQuery(id+"F0.wireOp",EDGE,"E21.filletArc");var subQ1=sQuery(id+"F0.wireOp",EDGE,"E7");var subQ2=sQuery(id+"F0.wireOp",EDGE,"E6");var subQ3=sQuery(id+"F0.wireOp",EDGE,"E5");var subQ4=sQuery(id+"F0.wireOp",EDGE,"E4");var subQ5=sQuery(id+"F0.wireOp",EDGE,"E22.filletArc");var subQ6=sQuery(id+"F0.wireOp",EDGE,"E1.bottom");var subQ7=sQuery(id+"F0.wireOp",EDGE,"E1.right");var subQ8=sQuery(id+"F0.wireOp",EDGE,"E1.top");var subQ9=sQuery(id+"F0.wireOp",EDGE,"E1.left");var subQ10=sQuery(id+"F0.wireOp",EDGE,"E23.filletArc");var subQ11=sQuery(id+"F0.wireOp",EDGE,"E24.filletArc");Q0=makeQuery(id+"F2.boolean.opBoolean","SPLIT",FACE,{"disambiguationData":[TD([makeQuery(id+"F1.opExtrude","SWEPT_FACE",FACE,{"disambiguationData":[OSD([subQ6])]})])],"derivedFrom":makeQuery(id+"F1.opExtrude","CAP_FACE",FACE,{"disambiguationData":[OSD([subQ6,subQ8,subQ9,subQ7,subQ4,subQ3,subQ2,subQ1,subQ0,subQ5,subQ10,subQ11])],"isStart":true})});}
            var sketch = newSketch(context, id + "F16", { "sketchPlane" : qUnion([Q0])});
            skLineSegment(sketch, "E79", {"start": v(-33, 74.25) * mm, "end": v(-15, 92.25) * mm});
            skLineSegment(sketch, "E80", {"start": v(-15, 92.25) * mm, "end": v(-15, 104.25) * mm});
            skArc(sketch, "E81", {"start": v(15, 104.25) * mm, "mid": v(0, 119.25) * mm, "end": v(-15, 104.25) * mm});
            skCircle(sketch, "E82", {"center": v(0, 104.25) * mm, "radius": 6 * mm});
            skLineSegment(sketch, "E83", {"start": v(0, 104.25) * mm, "end": v(0, 74.25) * mm, "construction": true});
            skLineSegment(sketch, "E84", {"start": v(-74.25, 0) * mm, "end": v(74.25, 0) * mm, "construction": true});
            skLineSegment(sketch, "E85.MirrorCS", {"start": v(-33, -74.25) * mm, "end": v(-15, -92.25) * mm});
            skLineSegment(sketch, "E86.MirrorCS", {"start": v(-15, -92.25) * mm, "end": v(-15, -104.25) * mm});
            skArc(sketch, "E87.MirrorCS", {"start": v(15, -104.25) * mm, "mid": v(0, -119.25) * mm, "end": v(-15, -104.25) * mm});
            skCircle(sketch, "E88.MirrorC", {"center": v(0, -104.25) * mm, "radius": 6 * mm});
            skLineSegment(sketch, "E89.MirrorCS", {"start": v(0, -104.25) * mm, "end": v(0, -74.25) * mm, "construction": true});
            skLineSegment(sketch, "E90", {"start": v(15, 104.25) * mm, "end": v(15, 92.25) * mm});
            skLineSegment(sketch, "E91", {"start": v(15, 92.25) * mm, "end": v(26.75, 74.25) * mm});
            skLineSegment(sketch, "E92.MirrorCS", {"start": v(15, -92.25) * mm, "end": v(26.75, -74.25) * mm});
            skLineSegment(sketch, "E93.MirrorCS", {"start": v(15, -104.25) * mm, "end": v(15, -92.25) * mm});
            skSolve(sketch);
        }
        {
            var Q0;
            Q0=makeQuery(id+"F16.imprint","IMPRINT",FACE,{"disambiguationData":[TD([[makeQuery(id+"F16.imprint","IMPRINT",EDGE,{"derivedFrom":makeQuery(id+"F1.opExtrude","CAP_EDGE",EDGE,{"disambiguationData":[OSD([sQuery(id+"F0.wireOp",EDGE,"E1.left")])],"isStart":true})}),-1.0]])]});
            var Q1;
            {var subQ0=sQuery(id+"F16.wireOp",EDGE,"E85.MirrorCS");Q1=makeQuery(id+"F16.imprint","IMPRINT",FACE,{"disambiguationData":[TD([[makeQuery(id+"F16.imprint","IMPRINT",EDGE,{"derivedFrom":subQ0}),1.0]])]});}
            var Q2;
            {var subQ0=sQuery(id+"F16.wireOp",EDGE,"E79");Q2=makeQuery(id+"F16.imprint","IMPRINT",FACE,{"disambiguationData":[TD([[makeQuery(id+"F16.imprint","IMPRINT",EDGE,{"derivedFrom":subQ0}),-1.0]])]});}
            var Q3;
            Q3 = qSketchRegion(id + "F0", true);
            var Q4;
            Q4=makeQuery(id+"F2.opExtrude","CAP_FACE",FACE,{"disambiguationData":[OSD([sQuery(id+"F0.wireOp",EDGE,"E12"),sQuery(id+"F0.wireOp",EDGE,"E13"),sQuery(id+"F0.wireOp",EDGE,"E14"),sQuery(id+"F0.wireOp",EDGE,"E15"),sQuery(id+"F0.wireOp",EDGE,"E17.filletArc"),sQuery(id+"F0.wireOp",EDGE,"E18.filletArc"),sQuery(id+"F0.wireOp",EDGE,"E19.filletArc"),sQuery(id+"F0.wireOp",EDGE,"E20.filletArc"),sQuery(id+"F0.wireOp",EDGE,"E25.0"),sQuery(id+"F0.wireOp",EDGE,"E25.1"),sQuery(id+"F0.wireOp",EDGE,"E25.2"),sQuery(id+"F0.wireOp",EDGE,"E25.3"),sQuery(id+"F0.wireOp",EDGE,"E25.4"),sQuery(id+"F0.wireOp",EDGE,"E25.5"),sQuery(id+"F0.wireOp",EDGE,"E25.6"),sQuery(id+"F0.wireOp",EDGE,"E25.7")])],"isStart":false});
            extrude(context, id + "F17", {"entities" : qUnion([Q0, Q1, Q2, Q3]), "operationType" : NewBodyOperationType.ADD, "endBound" : BoundingType.UP_TO_SURFACE, "depth" : 25 * mm, "endBoundEntityFace" : qUnion([Q4]), "offsetDistance" : 25 * mm});
        }
    });
